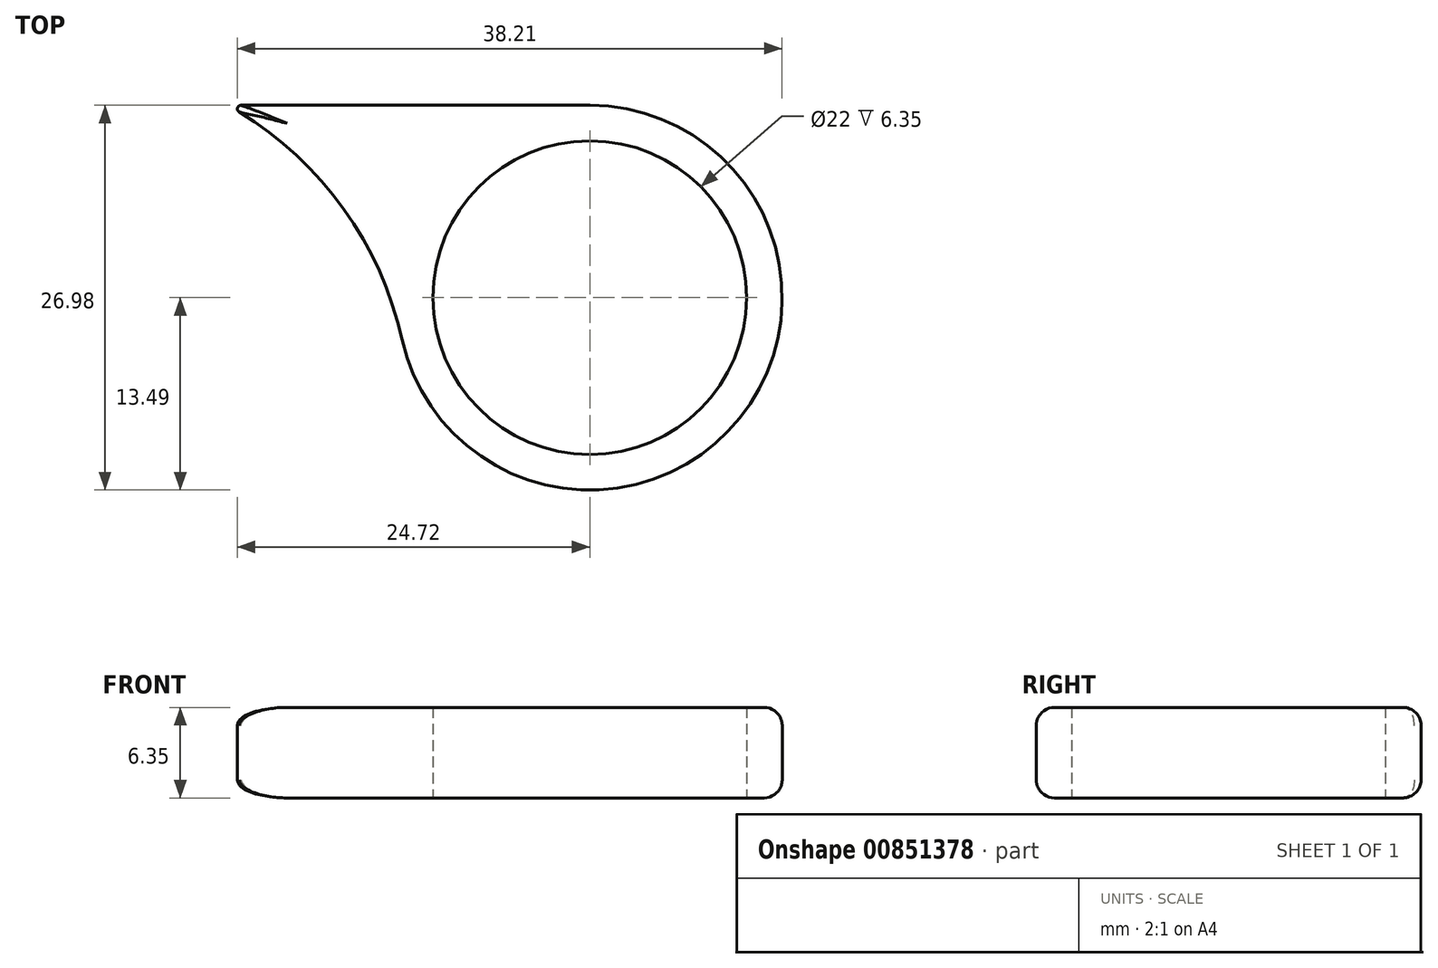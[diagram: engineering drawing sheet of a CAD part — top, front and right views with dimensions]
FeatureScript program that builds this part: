
annotation { "Feature Type Name" : "Feature", "Feature Type Description" : "" }
export const myFeature = defineFeature(function(context is Context, id is Id, definition is map)
    precondition{}
    {
        {
            var Q0;
            Q0=qCreatedBy(makeId("Top.planeOp"),FACE);
            var sketch = newSketch(context, id + "F0", { "sketchPlane" : qUnion([Q0])});
            skCircle(sketch, "E0", {"center": v(0, 0) * mm, "radius": 11 * mm});
            skCircle(sketch, "E1", {"center": v(0, 0) * mm, "radius": 13.5 * mm});
            skLineSegment(sketch, "E2", {"start": v(0, 13.5) * mm, "end": v(-25.4, 13.5) * mm});
            skArc(sketch, "E3", {"start": v(-13.17, -2.93) * mm, "mid": v(-17.53, 6.59) * mm, "end": v(-25.4, 13.5) * mm});
            skSolve(sketch);
        }
        {
            var Q0;
            Q0=makeQuery(id+"F0.imprint","IMPRINT",FACE,{"disambiguationData":[TD([[makeQuery(id+"F0.imprint","IMPRINT",EDGE,{"derivedFrom":sQuery(id+"F0.wireOp",EDGE,"E0")}),-1.0]])]});
            extrude(context, id + "F1", {"entities" : qUnion([Q0]), "depth" : 6.35 * mm, "offsetDistance" : 25.4 * mm});
        }
        {
            var Q0;
            Q0=qSketchRegion(id+"F0",true);
            extrude(context, id + "F2", {"entities" : qUnion([Q0]), "operationType" : NewBodyOperationType.ADD, "depth" : 6.35 * mm, "offsetDistance" : 25.4 * mm});
        }
        {
            var Q0;
            Q0=makeQuery(id+"F2.opExtrude","SWEPT_EDGE",EDGE,{"disambiguationData":[OSD([sQuery(id+"F0.wireOp",EDGE,"E2"),sQuery(id+"F0.wireOp",EDGE,"E3")])]});
            fillet(context, id + "F3", {"entities" : qUnion([Q0]), "radius" : 0.25 * mm, "tangentPropagation" : true, "allowEdgeOverflow" : false});
        }
        {
            var Q0;
            Q0=makeQuery(id+"F2.opExtrude","CAP_EDGE",EDGE,{"disambiguationData":[OSD([sQuery(id+"F0.wireOp",EDGE,"E2")])],"isStart":false});
            var Q1;
            Q1=makeQuery(id+"F2.opExtrude","CAP_EDGE",EDGE,{"disambiguationData":[OSD([sQuery(id+"F0.wireOp",EDGE,"E3")])],"isStart":false});
            fillet(context, id + "F4", {"entities" : qUnion([Q0, Q1]), "radius" : 1.27 * mm, "tangentPropagation" : true, "allowEdgeOverflow" : false});
        }
        {
            var Q0;
            Q0=makeQuery(id+"F1.opExtrude","CAP_EDGE",EDGE,{"disambiguationData":[OSD([sQuery(id+"F0.wireOp",EDGE,"E1")])],"isStart":true});
            var Q1;
            Q1=makeQuery(id+"F2.opExtrude","CAP_EDGE",EDGE,{"disambiguationData":[OSD([sQuery(id+"F0.wireOp",EDGE,"E3")])],"isStart":true});
            var Q2;
            Q2=makeQuery(id+"F2.opExtrude","CAP_EDGE",EDGE,{"disambiguationData":[OSD([sQuery(id+"F0.wireOp",EDGE,"E2")])],"isStart":true});
            fillet(context, id + "F5", {"entities" : qUnion([Q0, Q1, Q2]), "radius" : 1.27 * mm, "tangentPropagation" : true, "allowEdgeOverflow" : false});
        }
    });
